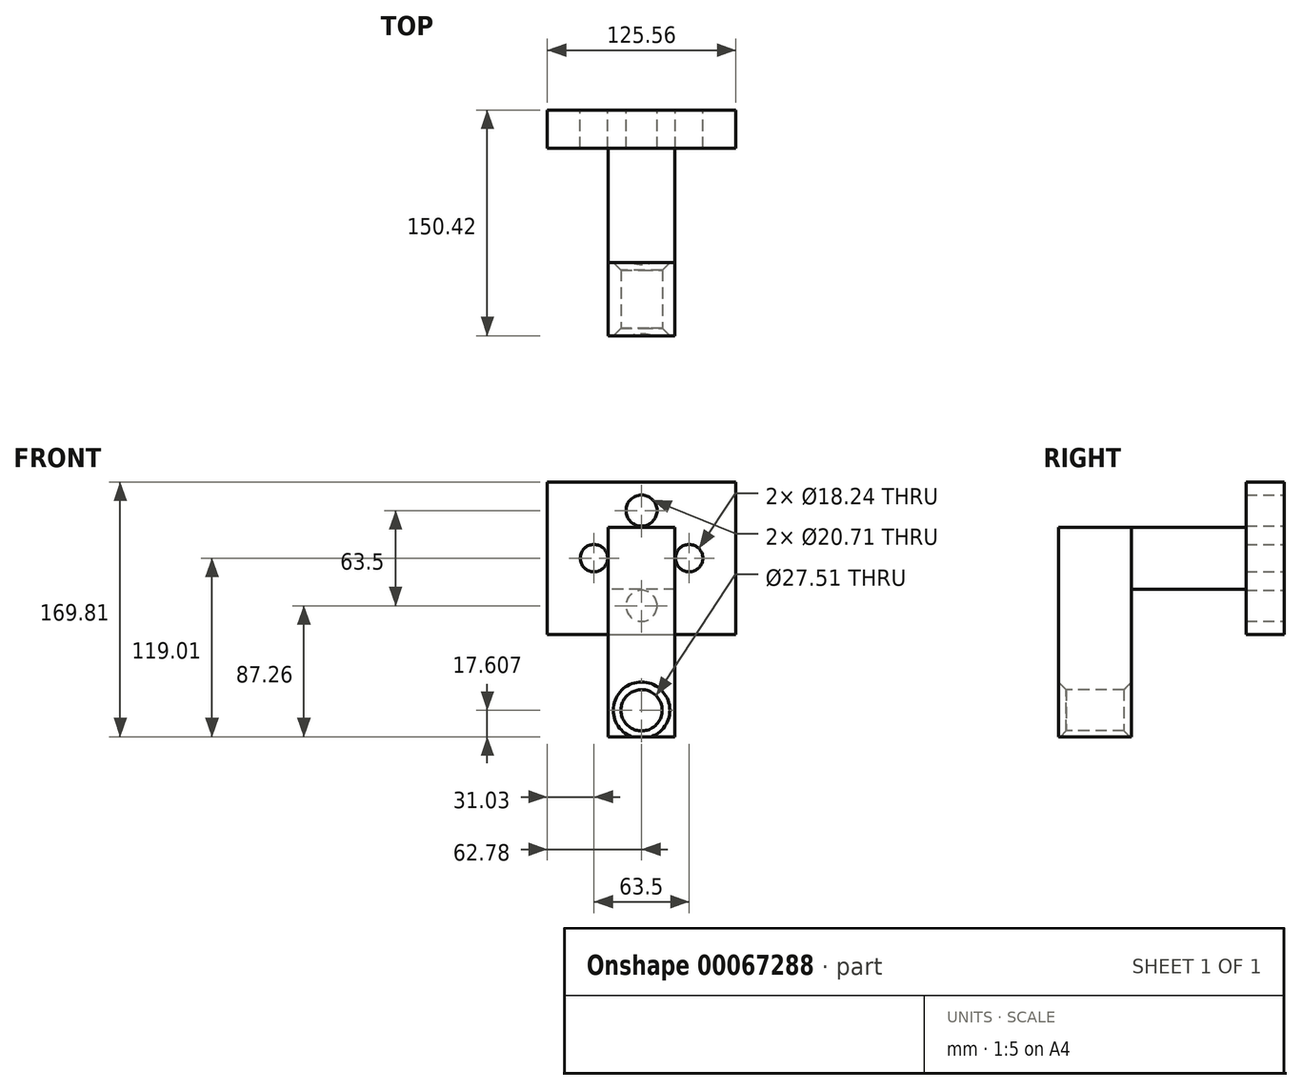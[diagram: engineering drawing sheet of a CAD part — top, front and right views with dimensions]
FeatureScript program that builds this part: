
annotation { "Feature Type Name" : "Feature", "Feature Type Description" : "" }
export const myFeature = defineFeature(function(context is Context, id is Id, definition is map)
    precondition{}
    {
        {
            var Q0;
            Q0=qCreatedBy(makeId("Front.planeOp"),FACE);
            var sketch = newSketch(context, id + "F0", { "sketchPlane" : qUnion([Q0])});
            skLineSegment(sketch, "E0.rect.bottom", {"start": v(-62.78, 50.8) * mm, "end": v(62.78, 50.8) * mm});
            skLineSegment(sketch, "E0.rect.top", {"start": v(-62.78, -50.8) * mm, "end": v(62.78, -50.8) * mm});
            skLineSegment(sketch, "E0.rect.left", {"start": v(-62.78, 50.8) * mm, "end": v(-62.78, -50.8) * mm});
            skLineSegment(sketch, "E0.rect.right", {"start": v(62.78, 50.8) * mm, "end": v(62.78, -50.8) * mm});
            skPoint(sketch, "E0.rect.middle", {"position": v(0, 0) * mm});
            skCircle(sketch, "E1", {"center": v(-31.75, 0) * mm, "radius": 9.12 * mm});
            skCircle(sketch, "E2.MirrorC", {"center": v(31.75, 0) * mm, "radius": 9.12 * mm});
            skCircle(sketch, "E3", {"center": v(0, 31.75) * mm, "radius": 10.35 * mm});
            skCircle(sketch, "E4.MirrorC", {"center": v(0, -31.75) * mm, "radius": 10.35 * mm});
            skLineSegment(sketch, "E5.rect.bottom", {"start": v(22.24, 20.7) * mm, "end": v(-22.24, 20.7) * mm});
            skLineSegment(sketch, "E5.rect.top", {"start": v(22.24, -20.7) * mm, "end": v(-22.24, -20.7) * mm});
            skLineSegment(sketch, "E5.rect.left", {"start": v(22.24, 20.7) * mm, "end": v(22.24, -20.7) * mm});
            skLineSegment(sketch, "E5.rect.right", {"start": v(-22.24, 20.7) * mm, "end": v(-22.24, -20.7) * mm});
            skSolve(sketch);
        }
        {
            var Q0;
            Q0 = qSketchRegion(id + "F0", true);
            extrude(context, id + "F1", {"entities" : qUnion([Q0]), "depth" : 25.4 * mm});
        }
        {
            var Q0;
            Q0=makeQuery(id+"F0.imprint","IMPRINT",FACE,{"disambiguationData":[TD([[makeQuery(id+"F0.imprint","IMPRINT",EDGE,{"derivedFrom":sQuery(id+"F0.wireOp",EDGE,"E5.rect.bottom")}),1.0]])]});
            extrude(context, id + "F2", {"entities" : qUnion([Q0]), "operationType" : NewBodyOperationType.ADD, "depth" : 101.6 * mm});
        }
        {
            var Q0;
            Q0=makeQuery(id+"F2.opExtrude","SWEPT_FACE",FACE,{"disambiguationData":[OSD([sQuery(id+"F0.wireOp",EDGE,"E5.rect.bottom")])]});
            var sketch = newSketch(context, id + "F3", { "sketchPlane" : qUnion([Q0])});
            skLineSegment(sketch, "E6.bottom", {"start": v(22.24, -101.6) * mm, "end": v(-22.24, -101.6) * mm});
            skLineSegment(sketch, "E6.top", {"start": v(22.24, -150.42) * mm, "end": v(-22.24, -150.42) * mm});
            skLineSegment(sketch, "E6.left", {"start": v(22.24, -101.6) * mm, "end": v(22.24, -150.42) * mm});
            skLineSegment(sketch, "E6.right", {"start": v(-22.24, -101.6) * mm, "end": v(-22.24, -150.42) * mm});
            skSolve(sketch);
        }
        {
            var Q0;
            Q0=makeQuery(id+"F3.imprint","IMPRINT",FACE,{"disambiguationData":[TD([[makeQuery(id+"F3.imprint","IMPRINT",EDGE,{"derivedFrom":sQuery(id+"F3.wireOp",EDGE,"E6.bottom")}),1.0]])]});
            extrude(context, id + "F4", {"entities" : qUnion([Q0]), "oppositeDirection" : true, "depth" : 139.7 * mm});
        }
        {
            var Q0;
            Q0=makeQuery(id+"F4.opExtrude","SWEPT_FACE",FACE,{"disambiguationData":[OSD([sQuery(id+"F3.wireOp",EDGE,"E6.top")])]});
            var sketch = newSketch(context, id + "F5", { "sketchPlane" : qUnion([Q0])});
            skCircle(sketch, "E7", {"center": v(0, -101.4) * mm, "radius": 13.76 * mm});
            skSolve(sketch);
        }
        {
            var Q0;
            Q0=makeQuery(id+"F5.imprint","IMPRINT",FACE,{"disambiguationData":[TD([[makeQuery(id+"F5.imprint","IMPRINT",EDGE,{"derivedFrom":sQuery(id+"F5.wireOp",EDGE,"E7")}),1.0]])]});
            extrude(context, id + "F6", {"entities" : qUnion([Q0]), "operationType" : NewBodyOperationType.REMOVE, "endBound" : BoundingType.THROUGH_ALL, "oppositeDirection" : true, "depth" : 25.4 * mm});
        }
        {
            var Q0;
            Q0=makeQuery(id+"F6.boolean.opBoolean","COPY",FACE,{"derivedFrom":makeQuery(id+"F6.opExtrude","SWEPT_FACE",FACE,{"disambiguationData":[OSD([sQuery(id+"F5.wireOp",EDGE,"E7")])]})});
            chamfer(context, id + "F7", {"entities" : qUnion([Q0]), "width" : 5.08 * mm, "tangentPropagation" : true});
        }
    });
